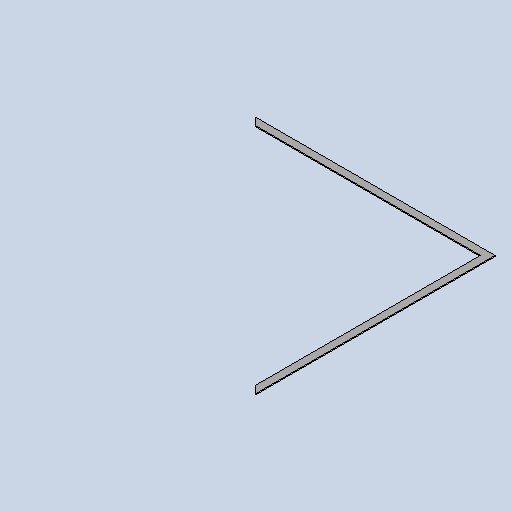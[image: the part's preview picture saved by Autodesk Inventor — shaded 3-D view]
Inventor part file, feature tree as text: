
AUTODESK INVENTOR PART (.ipt)
format: ipt  version: 2025.3 (Build 293356030, 356C)  size: 119,808 bytes
history: native  units: mm
features: other x3, sheet_metal_op x1, sketch x1
ambient origin geometry x8: Origin, YZ Plane, XZ Plane, XY Plane, X Axis, Y Axis, Z Axis, Center Point
bodies: Solid1 (feature_tree)
feature tree (5):
  sheet_metal_op  "Face1"
  other  "Corner Chamfer1"
  sketch  "Sketch1"  dims[d1=489.0mm d3=2.0mm d4=1.0mm d5=6.0mm d6=45.0deg d18=15.0mm d19=489.0mm]
  other  "Plate1"
  other  "Definition1"
